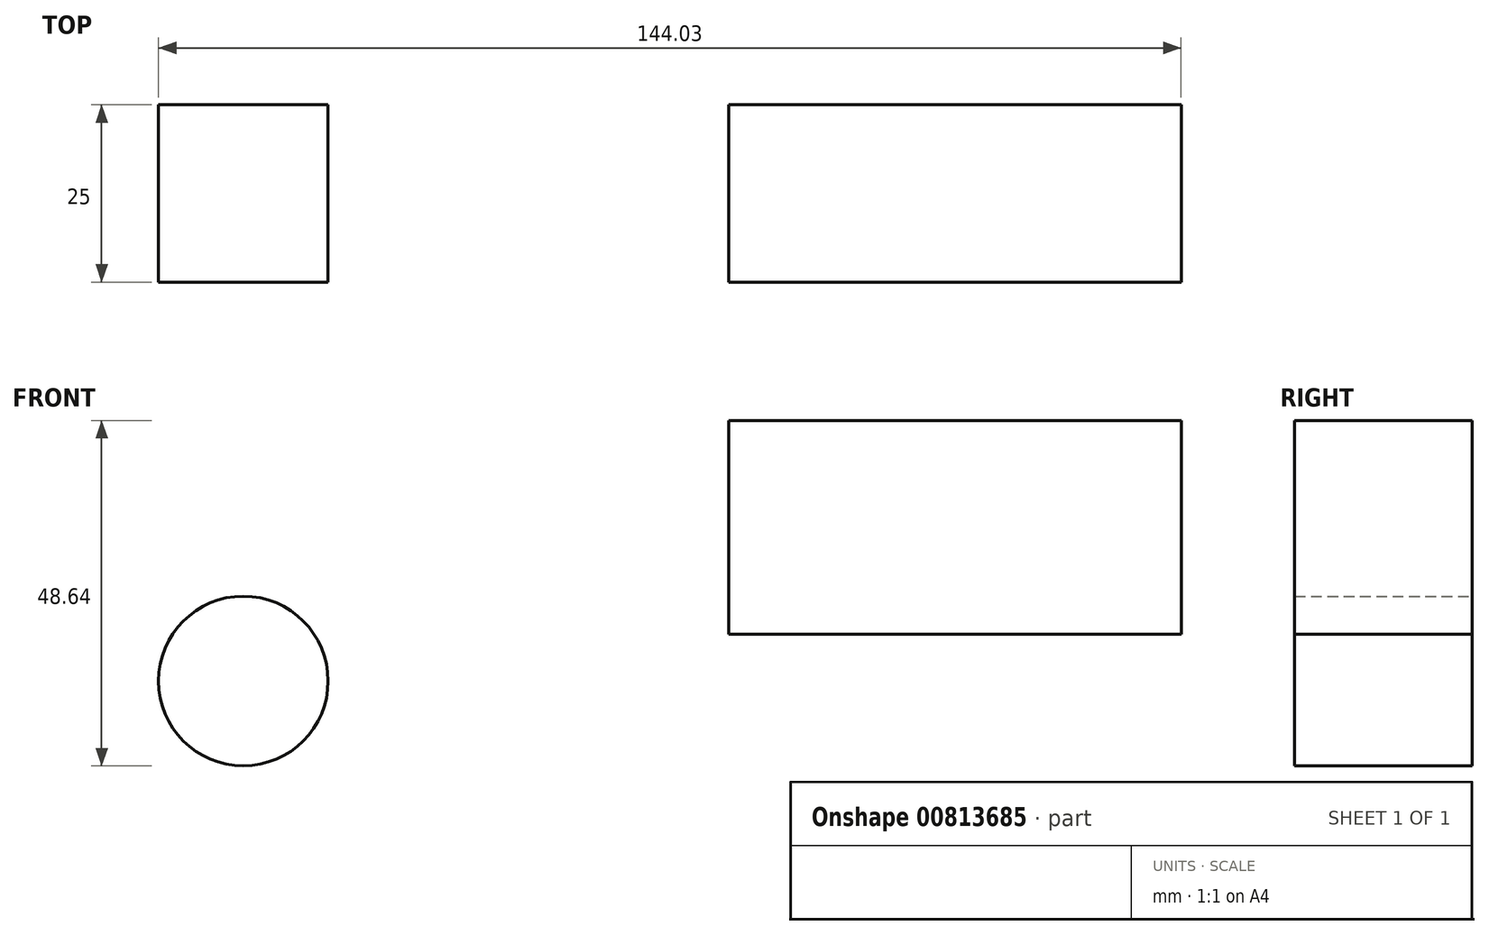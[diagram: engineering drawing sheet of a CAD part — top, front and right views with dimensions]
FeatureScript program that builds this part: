
annotation { "Feature Type Name" : "Feature", "Feature Type Description" : "" }
export const myFeature = defineFeature(function(context is Context, id is Id, definition is map)
    precondition{}
    {
        {
            var Q0;
            Q0=qCreatedBy(makeId("Front.planeOp"),FACE);
            var sketch = newSketch(context, id + "F0", { "sketchPlane" : qUnion([Q0])});
            skCircle(sketch, "E0", {"center": v(-158.98, 10.95) * mm, "radius": 11.94 * mm});
            skLineSegment(sketch, "E1.bottom", {"start": v(-90.6, 47.64) * mm, "end": v(-26.89, 47.64) * mm});
            skLineSegment(sketch, "E1.top", {"start": v(-90.6, 17.52) * mm, "end": v(-26.89, 17.52) * mm});
            skLineSegment(sketch, "E1.left", {"start": v(-90.6, 47.64) * mm, "end": v(-90.6, 17.52) * mm});
            skLineSegment(sketch, "E1.right", {"start": v(-26.89, 47.64) * mm, "end": v(-26.89, 17.52) * mm});
            skSolve(sketch);
        }
        {
            var Q0;
            Q0 = qSketchRegion(id + "F0", true);
            extrude(context, id + "F1", {"entities" : qUnion([Q0]), "depth" : 25 * mm, "offsetDistance" : 25 * mm});
        }
    });
